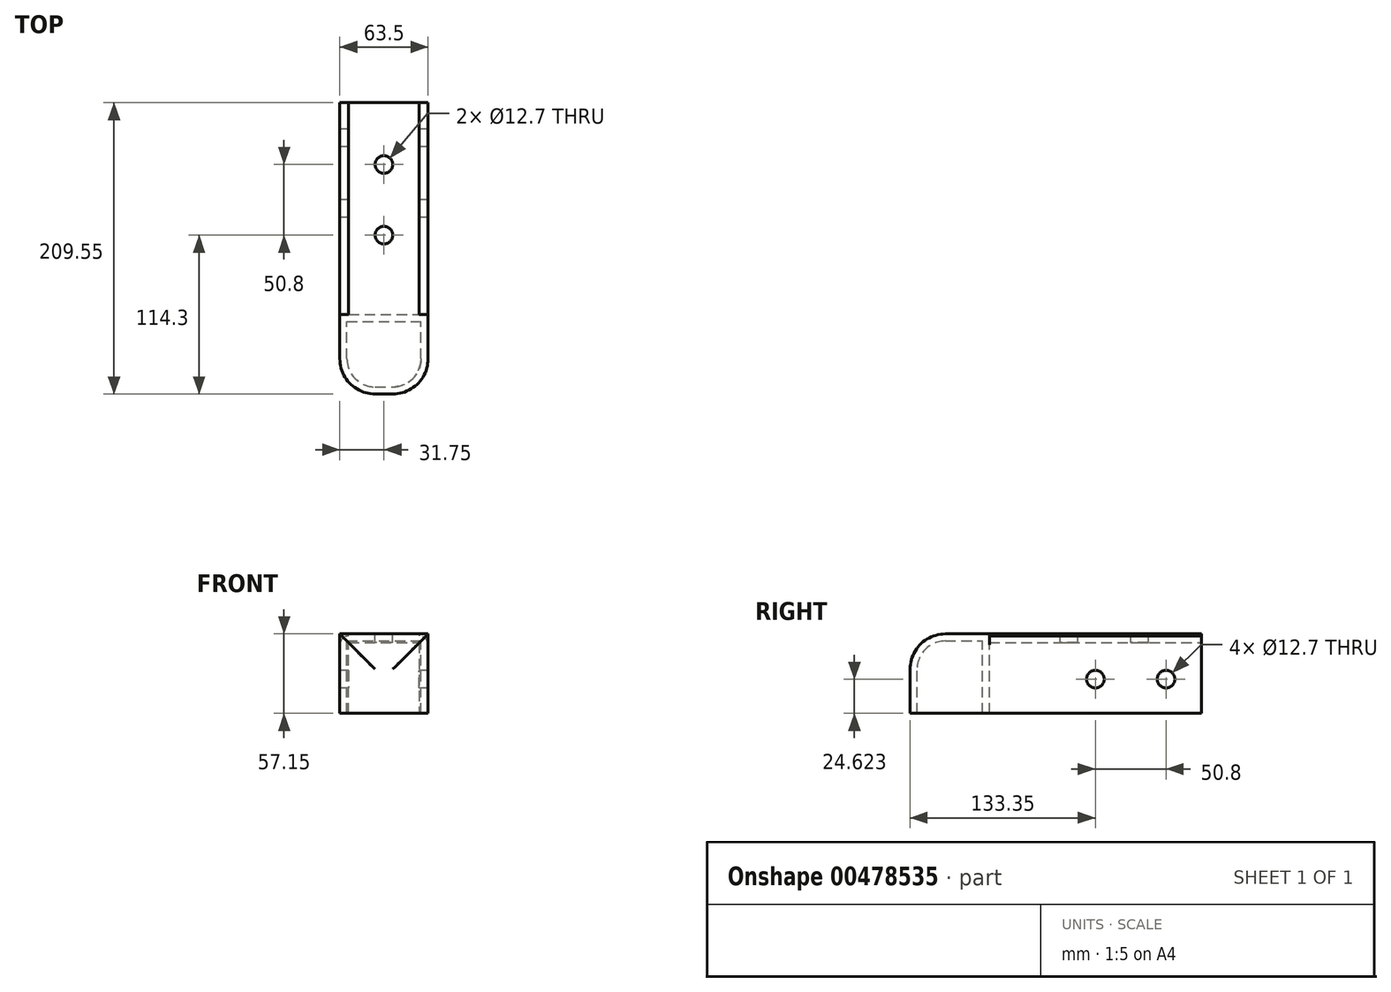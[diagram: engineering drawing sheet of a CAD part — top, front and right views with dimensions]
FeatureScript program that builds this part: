
annotation { "Feature Type Name" : "Feature", "Feature Type Description" : "" }
export const myFeature = defineFeature(function(context is Context, id is Id, definition is map)
    precondition{}
    {
        {
            var Q0;
            Q0=qCreatedBy(makeId("Front.planeOp"),FACE);
            var sketch = newSketch(context, id + "F0", { "sketchPlane" : qUnion([Q0])});
            skLineSegment(sketch, "E0", {"start": v(0, 0) * mm, "end": v(6.35, 0) * mm});
            skLineSegment(sketch, "E1", {"start": v(6.35, 0) * mm, "end": v(6.35, 50.8) * mm});
            skLineSegment(sketch, "E2", {"start": v(6.35, 50.8) * mm, "end": v(57.15, 50.8) * mm});
            skLineSegment(sketch, "E3", {"start": v(57.15, 50.8) * mm, "end": v(57.15, 0) * mm});
            skLineSegment(sketch, "E4", {"start": v(57.15, 0) * mm, "end": v(63.5, 0) * mm});
            skLineSegment(sketch, "E5", {"start": v(63.5, 0) * mm, "end": v(63.5, 49.25) * mm});
            skLineSegment(sketch, "E6", {"start": v(0, 49.25) * mm, "end": v(0, 0) * mm});
            skLineSegment(sketch, "E7", {"start": v(6.35, 55.6) * mm, "end": v(6.35, 55.6) * mm});
            skLineSegment(sketch, "E8", {"start": v(6.35, 55.6) * mm, "end": v(6.35, 57.15) * mm});
            skLineSegment(sketch, "E9", {"start": v(6.35, 57.15) * mm, "end": v(57.15, 57.15) * mm});
            skLineSegment(sketch, "E10", {"start": v(57.15, 57.15) * mm, "end": v(57.15, 55.6) * mm});
            skLineSegment(sketch, "E11", {"start": v(57.15, 55.6) * mm, "end": v(57.15, 55.6) * mm});
            skPoint(sketch, "E12.visualSharp", {"position": v(0, 55.6) * mm});
            skArc(sketch, "E12.filletArc", {"start": v(6.35, 55.6) * mm, "mid": v(1.86, 53.74) * mm, "end": v(0, 49.25) * mm});
            skPoint(sketch, "E13.visualSharp", {"position": v(63.5, 55.6) * mm});
            skArc(sketch, "E13.filletArc", {"start": v(63.5, 49.25) * mm, "mid": v(61.64, 53.74) * mm, "end": v(57.15, 55.6) * mm});
            skSolve(sketch);
        }
        {
            var Q0;
            Q0=makeQuery(id+"F0.imprint","IMPRINT",FACE,{"disambiguationData":[TD([[makeQuery(id+"F0.imprint","IMPRINT",EDGE,{"derivedFrom":sQuery(id+"F0.wireOp",EDGE,"E0")}),1.0]])]});
            extrude(context, id + "F1", {"entities" : qUnion([Q0]), "depth" : 152.4 * mm});
        }
        {
            var Q0;
            Q0=makeQuery(id+"F1.opExtrude","CAP_FACE",FACE,{"disambiguationData":[OSD([sQuery(id+"F0.wireOp",EDGE,"E0"),sQuery(id+"F0.wireOp",EDGE,"E1"),sQuery(id+"F0.wireOp",EDGE,"E2"),sQuery(id+"F0.wireOp",EDGE,"E3"),sQuery(id+"F0.wireOp",EDGE,"E4"),sQuery(id+"F0.wireOp",EDGE,"E5"),sQuery(id+"F0.wireOp",EDGE,"E6"),sQuery(id+"F0.wireOp",EDGE,"E8"),sQuery(id+"F0.wireOp",EDGE,"E9"),sQuery(id+"F0.wireOp",EDGE,"E10"),sQuery(id+"F0.wireOp",EDGE,"E12.filletArc"),sQuery(id+"F0.wireOp",EDGE,"E13.filletArc")])],"isStart":false});
            var sketch = newSketch(context, id + "F2", { "sketchPlane" : qUnion([Q0])});
            skLineSegment(sketch, "E14.bottom", {"start": v(0, 0) * mm, "end": v(63.5, 0) * mm});
            skLineSegment(sketch, "E14.top", {"start": v(0, 57.15) * mm, "end": v(63.5, 57.15) * mm});
            skLineSegment(sketch, "E14.left", {"start": v(0, 0) * mm, "end": v(0, 57.15) * mm});
            skLineSegment(sketch, "E14.right", {"start": v(63.5, 0) * mm, "end": v(63.5, 57.15) * mm});
            skSolve(sketch);
        }
        {
            var Q0;
            {var subQ0=makeQuery(id+"F1.opExtrude","CAP_EDGE",EDGE,{"disambiguationData":[OSD([sQuery(id+"F0.wireOp",EDGE,"E1")])],"isStart":false});Q0=makeQuery(id+"F2.imprint","IMPRINT",FACE,{"disambiguationData":[TD([[makeQuery(id+"F2.imprint","IMPRINT",EDGE,{"derivedFrom":subQ0}),1.0]])]});}
            var Q1;
            {var subQ1=makeQuery(id+"F1.opExtrude","CAP_EDGE",EDGE,{"disambiguationData":[OSD([sQuery(id+"F0.wireOp",EDGE,"E8")])],"isStart":false});Q1=makeQuery(id+"F2.imprint","IMPRINT",FACE,{"disambiguationData":[TD([[makeQuery(id+"F2.imprint","IMPRINT",EDGE,{"derivedFrom":subQ1}),1.0]])]});}
            var Q2;
            {var subQ1=makeQuery(id+"F1.opExtrude","CAP_EDGE",EDGE,{"disambiguationData":[OSD([sQuery(id+"F0.wireOp",EDGE,"E10")])],"isStart":false});Q2=makeQuery(id+"F2.imprint","IMPRINT",FACE,{"disambiguationData":[TD([[makeQuery(id+"F2.imprint","IMPRINT",EDGE,{"derivedFrom":subQ1}),1.0]])]});}
            var Q3;
            {var subQ1=makeQuery(id+"F1.opExtrude","CAP_EDGE",EDGE,{"disambiguationData":[OSD([sQuery(id+"F0.wireOp",EDGE,"E1")])],"isStart":false});Q3=makeQuery(id+"F2.imprint","IMPRINT",FACE,{"disambiguationData":[TD([[makeQuery(id+"F2.imprint","IMPRINT",EDGE,{"derivedFrom":subQ1}),-1.0]])]});}
            extrude(context, id + "F3", {"entities" : qUnion([Q0, Q1, Q2, Q3]), "operationType" : NewBodyOperationType.ADD, "depth" : 57.15 * mm});
        }
        {
            var Q0;
            Q0=makeQuery(id+"F3.opExtrude","CAP_EDGE",EDGE,{"disambiguationData":[OSD([sQuery(id+"F2.wireOp",EDGE,"E14.top")])],"isStart":false});
            var Q1;
            Q1=makeQuery(id+"F3.opExtrude","CAP_EDGE",EDGE,{"disambiguationData":[OSD([sQuery(id+"F2.wireOp",EDGE,"E14.left")])],"isStart":false});
            var Q2;
            Q2=makeQuery(id+"F3.opExtrude","CAP_EDGE",EDGE,{"disambiguationData":[OSD([sQuery(id+"F2.wireOp",EDGE,"E14.right")])],"isStart":false});
            fillet(context, id + "F4", {"entities" : qUnion([Q0, Q1, Q2]), "radius" : 25.4 * mm, "tangentPropagation" : true, "allowEdgeOverflow" : false});
        }
        {
            var Q0;
            Q0=makeQuery(id+"F3.boolean.opBoolean","MERGE",FACE,{"derivedFrom":[makeQuery(id+"F1.opExtrude","SWEPT_FACE",FACE,{"disambiguationData":[OSD([sQuery(id+"F0.wireOp",EDGE,"E0")])]}),makeQuery(id+"F1.opExtrude","SWEPT_FACE",FACE,{"disambiguationData":[OSD([sQuery(id+"F0.wireOp",EDGE,"E4")])]}),makeQuery(id+"F3.opExtrude","SWEPT_FACE",FACE,{"disambiguationData":[OSD([sQuery(id+"F2.wireOp",EDGE,"E14.bottom")])]})]});
            shell(context, id + "F5", {"entities" : qUnion([Q0]), "thickness" : 5.08 * mm});
        }
        {
            var Q0;
            Q0=makeQuery(id+"F3.boolean.opBoolean","MERGE",FACE,{"derivedFrom":[makeQuery(id+"F1.opExtrude","SWEPT_FACE",FACE,{"disambiguationData":[OSD([sQuery(id+"F0.wireOp",EDGE,"E6")])]}),makeQuery(id+"F3.opExtrude","SWEPT_FACE",FACE,{"disambiguationData":[OSD([sQuery(id+"F2.wireOp",EDGE,"E14.left")])]})]});
            var sketch = newSketch(context, id + "F6", { "sketchPlane" : qUnion([Q0])});
            skCircle(sketch, "E15", {"center": v(25.4, 24.62) * mm, "radius": 6.35 * mm});
            skPoint(sketch, "E15.centerSnap0", {"position": v(0, 24.62) * mm});
            skCircle(sketch, "E16", {"center": v(76.2, 24.62) * mm, "radius": 6.35 * mm});
            skSolve(sketch);
        }
        {
            var Q0;
            Q0=makeQuery(id+"F6.imprint","IMPRINT",FACE,{"disambiguationData":[TD([[makeQuery(id+"F6.imprint","IMPRINT",EDGE,{"derivedFrom":sQuery(id+"F6.wireOp",EDGE,"E15")}),1.0]])]});
            var Q1;
            Q1=makeQuery(id+"F6.imprint","IMPRINT",FACE,{"disambiguationData":[TD([[makeQuery(id+"F6.imprint","IMPRINT",EDGE,{"derivedFrom":sQuery(id+"F6.wireOp",EDGE,"E16")}),1.0]])]});
            extrude(context, id + "F7", {"entities" : qUnion([Q0, Q1]), "operationType" : NewBodyOperationType.REMOVE, "endBound" : BoundingType.THROUGH_ALL, "oppositeDirection" : true, "depth" : 25.4 * mm});
        }
        {
            var Q0;
            Q0=makeQuery(id+"F3.boolean.opBoolean","MERGE",FACE,{"derivedFrom":[makeQuery(id+"F1.opExtrude","SWEPT_FACE",FACE,{"disambiguationData":[OSD([sQuery(id+"F0.wireOp",EDGE,"E9")])]}),makeQuery(id+"F3.opExtrude","SWEPT_FACE",FACE,{"disambiguationData":[OSD([sQuery(id+"F2.wireOp",EDGE,"E14.top")])]})]});
            var sketch = newSketch(context, id + "F8", { "sketchPlane" : qUnion([Q0])});
            skCircle(sketch, "E17", {"center": v(31.75, -44.45) * mm, "radius": 6.35 * mm});
            skPoint(sketch, "E17.centerSnap0", {"position": v(31.75, 0) * mm});
            skCircle(sketch, "E18", {"center": v(31.75, -95.25) * mm, "radius": 6.35 * mm});
            skSolve(sketch);
        }
        {
            var Q0;
            Q0=makeQuery(id+"F8.imprint","IMPRINT",FACE,{"disambiguationData":[TD([[makeQuery(id+"F8.imprint","IMPRINT",EDGE,{"derivedFrom":sQuery(id+"F8.wireOp",EDGE,"E17")}),1.0]])]});
            var Q1;
            Q1=makeQuery(id+"F8.imprint","IMPRINT",FACE,{"disambiguationData":[TD([[makeQuery(id+"F8.imprint","IMPRINT",EDGE,{"derivedFrom":sQuery(id+"F8.wireOp",EDGE,"E18")}),1.0]])]});
            extrude(context, id + "F9", {"entities" : qUnion([Q0, Q1]), "operationType" : NewBodyOperationType.REMOVE, "endBound" : BoundingType.THROUGH_ALL, "oppositeDirection" : true, "depth" : 25.4 * mm});
        }
    });
